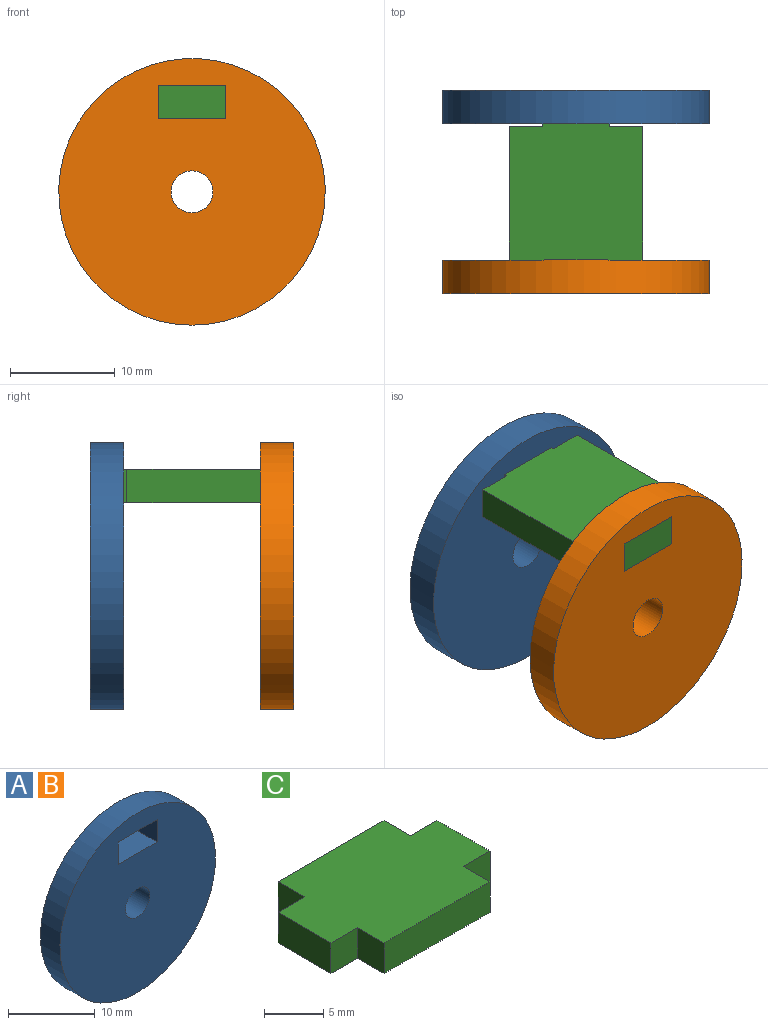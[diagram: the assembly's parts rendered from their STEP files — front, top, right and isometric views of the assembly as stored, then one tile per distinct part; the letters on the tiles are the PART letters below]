
ASSEMBLY  parts=3 mates=1
PART A: 8 faces, bbox 25.4x3.2x25.4 mm
  f0: cylinder r=1.99mm len=3.99mm, axis (0,1,0), area 39.8mm2, adj f2,f3
  f1: cylinder r=12.7mm len=25.4mm, axis (0,1,0), area 253.4mm2, adj f2,f3
  f2: plane 25.4x25.4mm, normal (0,-1,0), area 474.1mm2, adj f0,f1,f4,f5,f6,f7
  f3: plane 25.4x25.4mm, normal (0,1,0), area 474.1mm2, adj f0,f1,f4,f5,f6,f7
  f4: plane 6.35x3.18mm, normal (0,0,1), area 20.2mm2, adj f2,f3,f5,f7
  f5: plane 3.18x3.18mm, normal (-1,0,0), area 10.1mm2, adj f2,f3,f4,f6
  f6: plane 6.35x3.18mm, normal (0,0,-1), area 20.2mm2, adj f2,f3,f5,f7
  f7: plane 3.18x3.18mm, normal (1,0,0), area 10.1mm2, adj f2,f3,f4,f6
PART B: same geometry as A
PART C: 14 faces, bbox 19.1x12.7x3.2 mm
  f0: plane 3.18x3.18mm, normal (0,1,0), area 10.1mm2, adj f1,f3,f4,f12
  f1: plane 6.35x3.18mm, normal (-1,0,0), area 20.2mm2, adj f0,f2,f3,f4
  f2: plane 3.18x3.18mm, normal (0,-1,0), area 10.1mm2, adj f1,f3,f4,f5
  f3: plane 19.05x12.7mm, normal (0,0,1), area 201.6mm2, adj f0,f1,f2,f5,f6,f7,f8,f9
  f4: plane 19.05x12.7mm, normal (0,0,-1), area 201.6mm2, adj f0,f1,f2,f5,f6,f7,f8,f9
  f5: plane 3.18x3.18mm, normal (-1,0,0), area 10.1mm2, adj f2,f3,f4,f13
  f6: plane 3.18x3.18mm, normal (0,1,0), area 10.1mm2, adj f3,f4,f7,f10
  f7: plane 6.35x3.18mm, normal (1,0,0), area 20.2mm2, adj f3,f4,f6,f8
  f8: plane 3.18x3.18mm, normal (0,-1,0), area 10.1mm2, adj f3,f4,f7,f9
  f9: plane 3.18x3.18mm, normal (1,0,0), area 10.1mm2, adj f3,f4,f8,f13
  f10: plane 3.18x3.18mm, normal (1,0,0), area 10.1mm2, adj f3,f4,f6,f11
  f11: plane 12.7x3.18mm, normal (0,1,0), area 40.3mm2, adj f3,f4,f10,f12
  f12: plane 3.18x3.18mm, normal (-1,0,0), area 10.1mm2, adj f0,f3,f4,f11
  f13: plane 12.7x3.18mm, normal (0,-1,0), area 40.3mm2, adj f3,f4,f5,f9
PLACE A t=(0,16.18,0)mm
PLACE B at identity
PLACE C rot(axis=(0,0,-1),90deg) t=(0,6.35,6.99)mm
MATE parallel C.f6 <-> B.f5  axis (1,0,0) through (3.17,-1.59,8.57)mm
